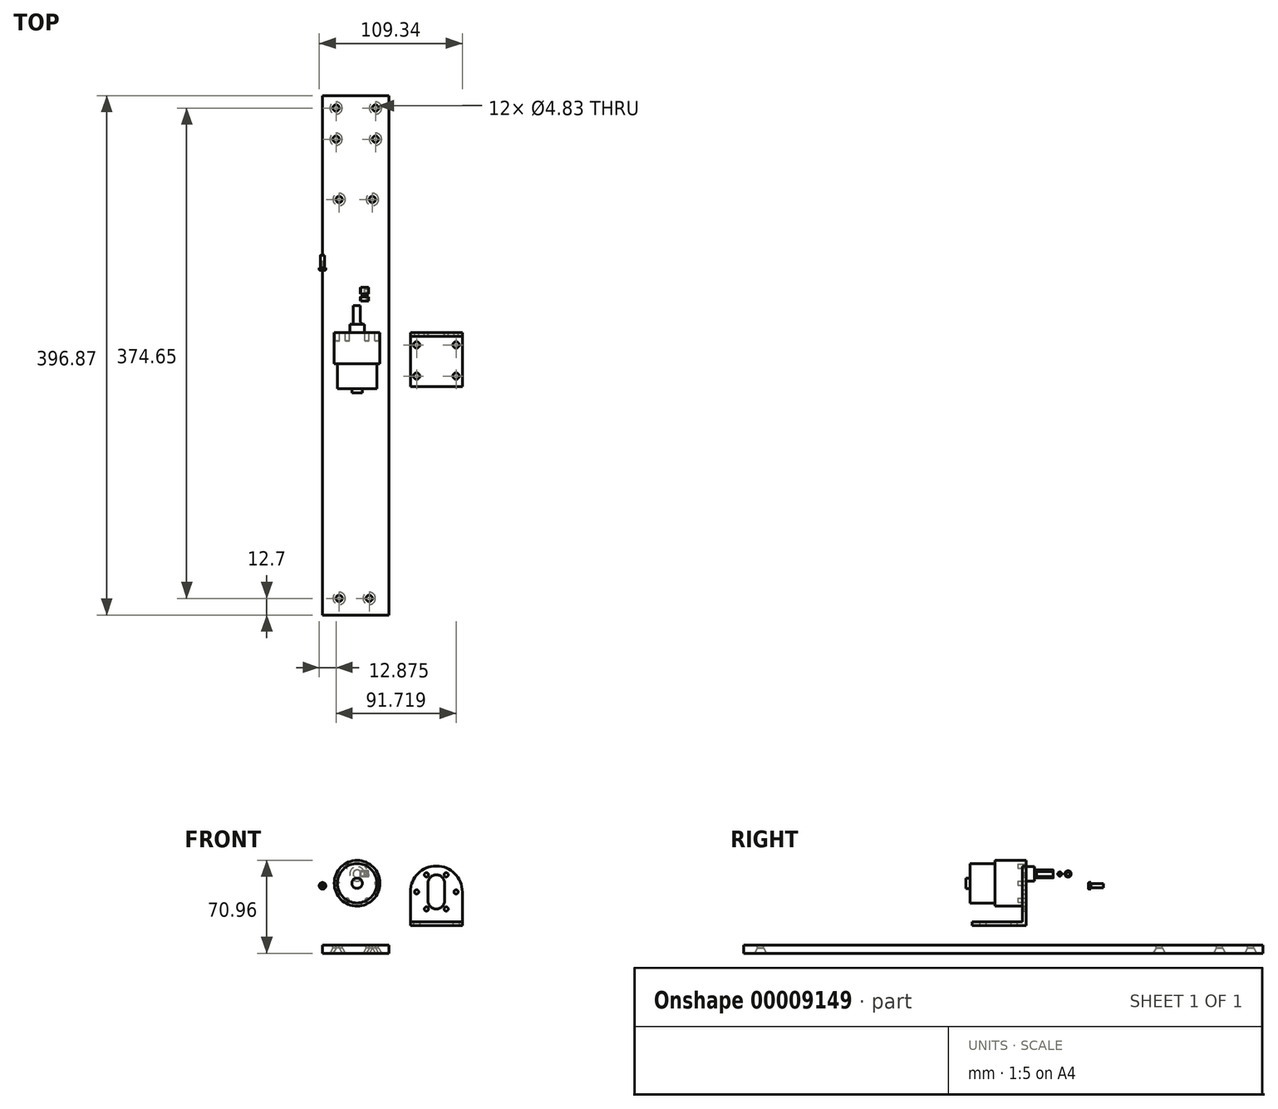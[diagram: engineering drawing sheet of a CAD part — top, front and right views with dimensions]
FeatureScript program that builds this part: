
annotation { "Feature Type Name" : "Feature", "Feature Type Description" : "" }
export const myFeature = defineFeature(function(context is Context, id is Id, definition is map)
    precondition{}
    {
        {
            var Q0;
            Q0=qCreatedBy(makeId("Front.planeOp"),FACE);
            var sketch = newSketch(context, id + "F0", { "sketchPlane" : qUnion([Q0])});
            skLineSegment(sketch, "E0.bottom", {"start": v(-48.57, -39.08) * mm, "end": v(2.23, -39.08) * mm});
            skLineSegment(sketch, "E0.top", {"start": v(-48.57, -45.43) * mm, "end": v(2.23, -45.43) * mm});
            skLineSegment(sketch, "E0.left", {"start": v(-48.57, -39.08) * mm, "end": v(-48.57, -45.43) * mm});
            skLineSegment(sketch, "E0.right", {"start": v(2.23, -39.08) * mm, "end": v(2.23, -45.43) * mm});
            skSolve(sketch);
        }
        {
            var Q0;
            Q0=makeQuery(id+"F0.imprint","IMPRINT",FACE,{"disambiguationData":[TD([[makeQuery(id+"F0.imprint","IMPRINT",EDGE,{"derivedFrom":sQuery(id+"F0.wireOp",EDGE,"E0.bottom")}),-1.0]])]});
            extrude(context, id + "F1", {"entities" : qUnion([Q0]), "depth" : 215.9 * mm, "hasSecondDirection" : true, "secondDirectionOppositeDirection" : true, "secondDirectionDepth" : 180.97 * mm});
        }
        {
            var Q0;
            Q0=makeQuery(id+"F1.opExtrude","SWEPT_FACE",FACE,{"disambiguationData":[OSD([sQuery(id+"F0.wireOp",EDGE,"E0.bottom")])]});
            var sketch = newSketch(context, id + "F2", { "sketchPlane" : qUnion([Q0])});
            skCircle(sketch, "E1", {"center": v(-10.47, 101.6) * mm, "radius": 2.41 * mm});
            skCircle(sketch, "E2", {"center": v(-35.87, 101.6) * mm, "radius": 2.41 * mm});
            skCircle(sketch, "E3", {"center": v(-12.89, -203.2) * mm, "radius": 2.41 * mm});
            skCircle(sketch, "E4", {"center": v(-35.87, -203.2) * mm, "radius": 2.41 * mm});
            skSolve(sketch);
        }
        {
            var Q0;
            Q0=makeQuery(id+"F2.imprint","IMPRINT",FACE,{"disambiguationData":[TD([[makeQuery(id+"F2.imprint","IMPRINT",EDGE,{"derivedFrom":sQuery(id+"F2.wireOp",EDGE,"E3")}),1.0]])]});
            var Q1;
            Q1=makeQuery(id+"F2.imprint","IMPRINT",FACE,{"disambiguationData":[TD([[makeQuery(id+"F2.imprint","IMPRINT",EDGE,{"derivedFrom":sQuery(id+"F2.wireOp",EDGE,"E4")}),1.0]])]});
            var Q2;
            Q2=makeQuery(id+"F2.imprint","IMPRINT",FACE,{"disambiguationData":[TD([[makeQuery(id+"F2.imprint","IMPRINT",EDGE,{"derivedFrom":sQuery(id+"F2.wireOp",EDGE,"E1")}),1.0]])]});
            var Q3;
            Q3=makeQuery(id+"F2.imprint","IMPRINT",FACE,{"disambiguationData":[TD([[makeQuery(id+"F2.imprint","IMPRINT",EDGE,{"derivedFrom":sQuery(id+"F2.wireOp",EDGE,"E2")}),1.0]])]});
            extrude(context, id + "F3", {"entities" : qUnion([Q0, Q1, Q2, Q3]), "operationType" : NewBodyOperationType.REMOVE, "endBound" : BoundingType.THROUGH_ALL, "oppositeDirection" : true, "depth" : 25.4 * mm});
        }
        {
            var Q0;
            Q0=qCreatedBy(makeId("Front.planeOp"),FACE);
            var sketch = newSketch(context, id + "F4", { "sketchPlane" : qUnion([Q0])});
            skLineSegment(sketch, "E5", {"start": v(53.48, 17.64) * mm, "end": v(53.48, -28.14) * mm, "construction": true});
            skLineSegment(sketch, "E6", {"start": v(23.33, 16.98) * mm, "end": v(23.33, -27.48) * mm, "construction": true});
            skLineSegment(sketch, "E7", {"start": v(38.4, 18.33) * mm, "end": v(38.4, -27.69) * mm, "construction": true});
            skCircle(sketch, "E8.cCircle", {"center": v(38.4, 1.46) * mm, "radius": 13.06 * mm, "construction": true});
            skLineSegment(sketch, "E8.0", {"start": v(30.87, 14.51) * mm, "end": v(45.95, 14.51) * mm, "construction": true});
            skLineSegment(sketch, "E8.1", {"start": v(45.95, 14.51) * mm, "end": v(53.48, 1.46) * mm, "construction": true});
            skLineSegment(sketch, "E8.2", {"start": v(53.48, 1.46) * mm, "end": v(45.95, -11.6) * mm, "construction": true});
            skLineSegment(sketch, "E8.3", {"start": v(45.95, -11.6) * mm, "end": v(30.87, -11.6) * mm, "construction": true});
            skLineSegment(sketch, "E8.4", {"start": v(30.87, -11.6) * mm, "end": v(23.33, 1.46) * mm, "construction": true});
            skLineSegment(sketch, "E8.5", {"start": v(23.33, 1.46) * mm, "end": v(30.87, 14.51) * mm, "construction": true});
            skPoint(sketch, "E8.0.midPoint", {"position": v(38.4, 14.51) * mm});
            skLineSegment(sketch, "E9", {"start": v(53.48, 14.51) * mm, "end": v(23.33, 14.51) * mm, "construction": true});
            skLineSegment(sketch, "E10", {"start": v(53.48, -11.6) * mm, "end": v(23.33, -11.6) * mm, "construction": true});
            skLineSegment(sketch, "E11", {"start": v(53.48, 8.16) * mm, "end": v(23.33, 8.16) * mm, "construction": true});
            skLineSegment(sketch, "E12", {"start": v(53.48, -5.25) * mm, "end": v(23.33, -5.25) * mm, "construction": true});
            skArc(sketch, "E13", {"start": v(44.76, 8.16) * mm, "mid": v(38.4, 14.51) * mm, "end": v(32.06, 8.16) * mm});
            skLineSegment(sketch, "E14", {"start": v(58.23, 1.46) * mm, "end": v(58.23, -24.3) * mm});
            skLineSegment(sketch, "E15", {"start": v(58.23, -24.3) * mm, "end": v(18.58, -24.3) * mm});
            skLineSegment(sketch, "E16", {"start": v(18.58, -24.3) * mm, "end": v(18.58, 1.46) * mm});
            skCircle(sketch, "E17", {"center": v(38.4, 1.46) * mm, "radius": 19.82 * mm});
            skLineSegment(sketch, "E18", {"start": v(44.76, 8.16) * mm, "end": v(44.76, -5.25) * mm});
            skLineSegment(sketch, "E19", {"start": v(32.06, 8.16) * mm, "end": v(32.06, -5.25) * mm});
            skArc(sketch, "E20", {"start": v(32.06, -5.25) * mm, "mid": v(38.4, -11.6) * mm, "end": v(44.76, -5.25) * mm});
            skCircle(sketch, "E21", {"center": v(45.95, 14.51) * mm, "radius": 1.59 * mm});
            skCircle(sketch, "E22", {"center": v(30.87, 14.51) * mm, "radius": 1.59 * mm});
            skCircle(sketch, "E23", {"center": v(45.95, -11.6) * mm, "radius": 1.59 * mm});
            skCircle(sketch, "E24", {"center": v(53.48, 1.46) * mm, "radius": 1.59 * mm});
            skCircle(sketch, "E25", {"center": v(23.33, 1.46) * mm, "radius": 1.59 * mm});
            skCircle(sketch, "E26", {"center": v(30.87, -11.6) * mm, "radius": 1.59 * mm});
            skSolve(sketch);
        }
        {
            var Q0;
            {var subQ2=sQuery(id+"F4.wireOp",EDGE,"E14");Q0=makeQuery(id+"F4.imprint","IMPRINT",FACE,{"disambiguationData":[TD([[makeQuery(id+"F4.imprint","IMPRINT",EDGE,{"derivedFrom":subQ2}),-1.0]])]});}
            var Q1;
            Q1=makeQuery(id+"F4.imprint","IMPRINT",FACE,{"disambiguationData":[TD([[makeQuery(id+"F4.imprint","IMPRINT",EDGE,{"derivedFrom":sQuery(id+"F4.wireOp",EDGE,"E13")}),-1.0]])]});
            extrude(context, id + "F5", {"entities" : qUnion([Q0, Q1]), "depth" : 3 * mm});
        }
        {
            var Q0;
            Q0=makeQuery(id+"F5.opExtrude","CAP_FACE",FACE,{"disambiguationData":[OSD([sQuery(id+"F4.wireOp",EDGE,"E13"),sQuery(id+"F4.wireOp",EDGE,"E14"),sQuery(id+"F4.wireOp",EDGE,"E15"),sQuery(id+"F4.wireOp",EDGE,"E16"),sQuery(id+"F4.wireOp",EDGE,"E17"),sQuery(id+"F4.wireOp",EDGE,"E18"),sQuery(id+"F4.wireOp",EDGE,"E19"),sQuery(id+"F4.wireOp",EDGE,"E20"),sQuery(id+"F4.wireOp",EDGE,"E21"),sQuery(id+"F4.wireOp",EDGE,"E22"),sQuery(id+"F4.wireOp",EDGE,"E23"),sQuery(id+"F4.wireOp",EDGE,"E24"),sQuery(id+"F4.wireOp",EDGE,"E25"),sQuery(id+"F4.wireOp",EDGE,"E26")])],"isStart":false});
            var sketch = newSketch(context, id + "F6", { "sketchPlane" : qUnion([Q0])});
            skLineSegment(sketch, "E27", {"start": v(18.58, -21.3) * mm, "end": v(58.23, -21.3) * mm});
            skSolve(sketch);
        }
        {
            var Q0;
            {var subQ1=sQuery(id+"F6.wireOp",EDGE,"E27");Q0=makeQuery(id+"F6.imprint","IMPRINT",FACE,{"disambiguationData":[TD([[makeQuery(id+"F6.imprint","IMPRINT",EDGE,{"derivedFrom":subQ1}),-1.0]])]});}
            extrude(context, id + "F7", {"entities" : qUnion([Q0]), "operationType" : NewBodyOperationType.ADD, "depth" : 38.28 * mm});
        }
        {
            var Q0;
            {var subQ0=sQuery(id+"F4.wireOp",EDGE,"E15");Q0=makeQuery(id+"F7.boolean.opBoolean","MERGE",FACE,{"derivedFrom":[makeQuery(id+"F5.opExtrude","SWEPT_FACE",FACE,{"disambiguationData":[OSD([subQ0])]}),makeQuery(id+"F7.opExtrude","SWEPT_FACE",FACE,{"disambiguationData":[OSD([subQ0])]})]});}
            var sketch = newSketch(context, id + "F8", { "sketchPlane" : qUnion([Q0])});
            skLineSegment(sketch, "E28", {"start": v(23.33, 41.27) * mm, "end": v(23.33, 0) * mm, "construction": true});
            skLineSegment(sketch, "E29", {"start": v(53.48, 41.27) * mm, "end": v(53.48, 0) * mm, "construction": true});
            skLineSegment(sketch, "E30", {"start": v(18.58, 33.35) * mm, "end": v(58.23, 33.35) * mm, "construction": true});
            skLineSegment(sketch, "E31", {"start": v(18.58, 9.55) * mm, "end": v(58.23, 9.55) * mm, "construction": true});
            skCircle(sketch, "E32", {"center": v(23.33, 33.35) * mm, "radius": 2.41 * mm});
            skCircle(sketch, "E33", {"center": v(53.48, 33.35) * mm, "radius": 2.41 * mm});
            skCircle(sketch, "E34", {"center": v(53.48, 9.55) * mm, "radius": 2.41 * mm});
            skCircle(sketch, "E35", {"center": v(23.33, 9.55) * mm, "radius": 2.41 * mm});
            skSolve(sketch);
        }
        {
            var Q0;
            Q0=makeQuery(id+"F8.imprint","IMPRINT",FACE,{"disambiguationData":[TD([[makeQuery(id+"F8.imprint","IMPRINT",EDGE,{"derivedFrom":sQuery(id+"F8.wireOp",EDGE,"E32")}),1.0]])]});
            var Q1;
            Q1=makeQuery(id+"F8.imprint","IMPRINT",FACE,{"disambiguationData":[TD([[makeQuery(id+"F8.imprint","IMPRINT",EDGE,{"derivedFrom":sQuery(id+"F8.wireOp",EDGE,"E33")}),1.0]])]});
            var Q2;
            Q2=makeQuery(id+"F8.imprint","IMPRINT",FACE,{"disambiguationData":[TD([[makeQuery(id+"F8.imprint","IMPRINT",EDGE,{"derivedFrom":sQuery(id+"F8.wireOp",EDGE,"E34")}),1.0]])]});
            var Q3;
            Q3=makeQuery(id+"F8.imprint","IMPRINT",FACE,{"disambiguationData":[TD([[makeQuery(id+"F8.imprint","IMPRINT",EDGE,{"derivedFrom":sQuery(id+"F8.wireOp",EDGE,"E35")}),1.0]])]});
            extrude(context, id + "F9", {"entities" : qUnion([Q0, Q1, Q2, Q3]), "operationType" : NewBodyOperationType.REMOVE, "endBound" : BoundingType.THROUGH_ALL, "oppositeDirection" : true, "depth" : 25.4 * mm});
        }
        {
            var Q0;
            Q0=qCreatedBy(makeId("Front.planeOp"),FACE);
            var sketch = newSketch(context, id + "F10", { "sketchPlane" : qUnion([Q0])});
            skCircle(sketch, "E36", {"center": v(-22.17, 8.07) * mm, "radius": 17.46 * mm});
            skSolve(sketch);
        }
        {
            var Q0;
            Q0=makeQuery(id+"F10.imprint","IMPRINT",FACE,{"disambiguationData":[TD([[makeQuery(id+"F10.imprint","IMPRINT",EDGE,{"derivedFrom":sQuery(id+"F10.wireOp",EDGE,"E36")}),1.0]])]});
            extrude(context, id + "F11", {"entities" : qUnion([Q0]), "depth" : 23.8 * mm});
        }
        {
            var Q0;
            Q0=makeQuery(id+"F11.opExtrude","CAP_FACE",FACE,{"disambiguationData":[OSD([sQuery(id+"F10.wireOp",EDGE,"E36")])],"isStart":true});
            var sketch = newSketch(context, id + "F12", { "sketchPlane" : qUnion([Q0])});
            skLineSegment(sketch, "E37", {"start": v(7.1, 16.89) * mm, "end": v(7.1, -0.74) * mm, "construction": true});
            skLineSegment(sketch, "E38", {"start": v(37.24, 16.89) * mm, "end": v(37.24, -0.74) * mm, "construction": true});
            skCircle(sketch, "E39.cCircle", {"center": v(22.17, 8.07) * mm, "radius": 13.06 * mm, "construction": true});
            skLineSegment(sketch, "E39.0", {"start": v(14.63, 21.13) * mm, "end": v(29.7, 21.13) * mm, "construction": true});
            skLineSegment(sketch, "E39.1", {"start": v(29.7, 21.13) * mm, "end": v(37.24, 8.07) * mm, "construction": true});
            skLineSegment(sketch, "E39.2", {"start": v(37.24, 8.07) * mm, "end": v(29.7, -4.98) * mm, "construction": true});
            skLineSegment(sketch, "E39.3", {"start": v(29.7, -4.98) * mm, "end": v(14.63, -4.98) * mm, "construction": true});
            skLineSegment(sketch, "E39.4", {"start": v(14.63, -4.98) * mm, "end": v(7.1, 8.07) * mm, "construction": true});
            skLineSegment(sketch, "E39.5", {"start": v(7.1, 8.07) * mm, "end": v(14.63, 21.13) * mm, "construction": true});
            skPoint(sketch, "E39.0.midPoint", {"position": v(22.17, 21.13) * mm});
            skCircle(sketch, "E40", {"center": v(14.63, 21.13) * mm, "radius": 1.59 * mm});
            skCircle(sketch, "E41", {"center": v(29.7, 21.13) * mm, "radius": 1.59 * mm});
            skCircle(sketch, "E42", {"center": v(37.24, 8.07) * mm, "radius": 1.59 * mm});
            skCircle(sketch, "E43", {"center": v(29.7, -4.98) * mm, "radius": 1.59 * mm});
            skCircle(sketch, "E44", {"center": v(14.63, -4.98) * mm, "radius": 1.59 * mm});
            skCircle(sketch, "E45", {"center": v(7.1, 8.07) * mm, "radius": 1.59 * mm});
            skLineSegment(sketch, "E46", {"start": v(22.17, 25.53) * mm, "end": v(22.17, -9.4) * mm, "construction": true});
            skSolve(sketch);
        }
        {
            var Q0;
            Q0=makeQuery(id+"F12.imprint","IMPRINT",FACE,{"disambiguationData":[TD([[makeQuery(id+"F12.imprint","IMPRINT",EDGE,{"derivedFrom":sQuery(id+"F12.wireOp",EDGE,"E40")}),1.0]])]});
            var Q1;
            Q1=makeQuery(id+"F12.imprint","IMPRINT",FACE,{"disambiguationData":[TD([[makeQuery(id+"F12.imprint","IMPRINT",EDGE,{"derivedFrom":sQuery(id+"F12.wireOp",EDGE,"E41")}),1.0]])]});
            var Q2;
            Q2=makeQuery(id+"F12.imprint","IMPRINT",FACE,{"disambiguationData":[TD([[makeQuery(id+"F12.imprint","IMPRINT",EDGE,{"derivedFrom":sQuery(id+"F12.wireOp",EDGE,"E42")}),1.0]])]});
            var Q3;
            Q3=makeQuery(id+"F12.imprint","IMPRINT",FACE,{"disambiguationData":[TD([[makeQuery(id+"F12.imprint","IMPRINT",EDGE,{"derivedFrom":sQuery(id+"F12.wireOp",EDGE,"E43")}),1.0]])]});
            var Q4;
            Q4=makeQuery(id+"F12.imprint","IMPRINT",FACE,{"disambiguationData":[TD([[makeQuery(id+"F12.imprint","IMPRINT",EDGE,{"derivedFrom":sQuery(id+"F12.wireOp",EDGE,"E44")}),1.0]])]});
            var Q5;
            Q5=makeQuery(id+"F12.imprint","IMPRINT",FACE,{"disambiguationData":[TD([[makeQuery(id+"F12.imprint","IMPRINT",EDGE,{"derivedFrom":sQuery(id+"F12.wireOp",EDGE,"E45")}),1.0]])]});
            extrude(context, id + "F13", {"entities" : qUnion([Q0, Q1, Q2, Q3, Q4, Q5]), "operationType" : NewBodyOperationType.REMOVE, "oppositeDirection" : true, "depth" : 6.35 * mm});
        }
        {
            var Q0;
            Q0=makeQuery(id+"F11.opExtrude","CAP_FACE",FACE,{"disambiguationData":[OSD([sQuery(id+"F10.wireOp",EDGE,"E36")])],"isStart":true});
            var sketch = newSketch(context, id + "F14", { "sketchPlane" : qUnion([Q0])});
            skLineSegment(sketch, "E47", {"start": v(6.24, 15.22) * mm, "end": v(38.1, 15.22) * mm, "construction": true});
            skLineSegment(sketch, "E48", {"start": v(22.17, 15.22) * mm, "end": v(22.17, 25.53) * mm, "construction": true});
            skCircle(sketch, "E49", {"center": v(22.17, 15.22) * mm, "radius": 5.55 * mm});
            skSolve(sketch);
        }
        {
            var Q0;
            Q0=makeQuery(id+"F14.imprint","IMPRINT",FACE,{"disambiguationData":[TD([[makeQuery(id+"F14.imprint","IMPRINT",EDGE,{"derivedFrom":sQuery(id+"F14.wireOp",EDGE,"E49")}),1.0]])]});
            extrude(context, id + "F15", {"entities" : qUnion([Q0]), "operationType" : NewBodyOperationType.ADD, "depth" : 6.35 * mm});
        }
        {
            var Q0;
            Q0=makeQuery(id+"F15.opExtrude","CAP_FACE",FACE,{"disambiguationData":[OSD([sQuery(id+"F14.wireOp",EDGE,"E49")])],"isStart":false});
            var sketch = newSketch(context, id + "F16", { "sketchPlane" : qUnion([Q0])});
            skCircle(sketch, "E50", {"center": v(22.17, 15.22) * mm, "radius": 3 * mm});
            skSolve(sketch);
        }
        {
            var Q0;
            Q0=makeQuery(id+"F16.imprint","IMPRINT",FACE,{"disambiguationData":[TD([[makeQuery(id+"F16.imprint","IMPRINT",EDGE,{"derivedFrom":sQuery(id+"F16.wireOp",EDGE,"E50")}),1.0]])]});
            extrude(context, id + "F17", {"entities" : qUnion([Q0]), "operationType" : NewBodyOperationType.ADD, "depth" : 14.27 * mm});
        }
        {
            var Q0;
            Q0=makeQuery(id+"F11.opExtrude","CAP_FACE",FACE,{"disambiguationData":[OSD([sQuery(id+"F10.wireOp",EDGE,"E36")])],"isStart":false});
            var sketch = newSketch(context, id + "F18", { "sketchPlane" : qUnion([Q0])});
            skCircle(sketch, "E51", {"center": v(-22.17, 8.07) * mm, "radius": 15.07 * mm});
            skSolve(sketch);
        }
        {
            var Q0;
            Q0=makeQuery(id+"F18.imprint","IMPRINT",FACE,{"disambiguationData":[TD([[makeQuery(id+"F18.imprint","IMPRINT",EDGE,{"derivedFrom":sQuery(id+"F18.wireOp",EDGE,"E51")}),1.0]])]});
            extrude(context, id + "F19", {"entities" : qUnion([Q0]), "operationType" : NewBodyOperationType.ADD, "depth" : 19.05 * mm});
        }
        {
            var Q0;
            Q0=makeQuery(id+"F19.opExtrude","CAP_FACE",FACE,{"disambiguationData":[OSD([sQuery(id+"F18.wireOp",EDGE,"E51")])],"isStart":false});
            var sketch = newSketch(context, id + "F20", { "sketchPlane" : qUnion([Q0])});
            skCircle(sketch, "E52", {"center": v(-22.17, 8.07) * mm, "radius": 3.96 * mm});
            skSolve(sketch);
        }
        {
            var Q0;
            Q0=makeQuery(id+"F20.imprint","IMPRINT",FACE,{"disambiguationData":[TD([[makeQuery(id+"F20.imprint","IMPRINT",EDGE,{"derivedFrom":sQuery(id+"F20.wireOp",EDGE,"E52")}),1.0]])]});
            extrude(context, id + "F21", {"entities" : qUnion([Q0]), "operationType" : NewBodyOperationType.ADD, "depth" : 3.17 * mm});
        }
        {
            var Q0;
            Q0=makeQuery(id+"F3.boolean.opBoolean","INTERSECT",EDGE,{"derivedFrom":[makeQuery(id+"F1.opExtrude","SWEPT_FACE",FACE,{"disambiguationData":[OSD([sQuery(id+"F0.wireOp",EDGE,"E0.top")])]}),makeQuery(id+"F3.opExtrude","SWEPT_FACE",FACE,{"disambiguationData":[OSD([sQuery(id+"F2.wireOp",EDGE,"E3")])]})]});
            var Q1;
            Q1=makeQuery(id+"F3.boolean.opBoolean","INTERSECT",EDGE,{"derivedFrom":[makeQuery(id+"F1.opExtrude","SWEPT_FACE",FACE,{"disambiguationData":[OSD([sQuery(id+"F0.wireOp",EDGE,"E0.top")])]}),makeQuery(id+"F3.opExtrude","SWEPT_FACE",FACE,{"disambiguationData":[OSD([sQuery(id+"F2.wireOp",EDGE,"E4")])]})]});
            var Q2;
            Q2=makeQuery(id+"F3.boolean.opBoolean","INTERSECT",EDGE,{"derivedFrom":[makeQuery(id+"F1.opExtrude","SWEPT_FACE",FACE,{"disambiguationData":[OSD([sQuery(id+"F0.wireOp",EDGE,"E0.top")])]}),makeQuery(id+"F3.opExtrude","SWEPT_FACE",FACE,{"disambiguationData":[OSD([sQuery(id+"F2.wireOp",EDGE,"E1")])]})]});
            var Q3;
            Q3=makeQuery(id+"F3.boolean.opBoolean","INTERSECT",EDGE,{"derivedFrom":[makeQuery(id+"F1.opExtrude","SWEPT_FACE",FACE,{"disambiguationData":[OSD([sQuery(id+"F0.wireOp",EDGE,"E0.top")])]}),makeQuery(id+"F3.opExtrude","SWEPT_FACE",FACE,{"disambiguationData":[OSD([sQuery(id+"F2.wireOp",EDGE,"E2")])]})]});
            chamfer(context, id + "F22", {"entities" : qUnion([Q0, Q1, Q2, Q3]), "chamferType" : ChamferType.OFFSET_ANGLE, "width" : 2.3 * mm, "oppositeDirection" : false, "angle" : 60 * degree, "tangentPropagation" : true});
        }
        {
            var Q0;
            Q0=makeQuery(id+"F1.opExtrude","SWEPT_FACE",FACE,{"disambiguationData":[OSD([sQuery(id+"F0.wireOp",EDGE,"E0.bottom")])]});
            var sketch = newSketch(context, id + "F23", { "sketchPlane" : qUnion([Q0])});
            skLineSegment(sketch, "E53", {"start": v(-23.17, 180.98) * mm, "end": v(-23.17, 91.89) * mm, "construction": true});
            skLineSegment(sketch, "E54", {"start": v(2.23, 171.45) * mm, "end": v(-48.57, 171.45) * mm, "construction": true});
            skLineSegment(sketch, "E55", {"start": v(2.23, 147.65) * mm, "end": v(-48.57, 147.65) * mm, "construction": true});
            skLineSegment(sketch, "E56", {"start": v(-8.11, 180.98) * mm, "end": v(-8.11, 120.47) * mm, "construction": true});
            skLineSegment(sketch, "E57", {"start": v(-38.24, 180.98) * mm, "end": v(-38.24, 116.54) * mm, "construction": true});
            skCircle(sketch, "E58", {"center": v(-8.11, 171.45) * mm, "radius": 2.41 * mm});
            skCircle(sketch, "E59", {"center": v(-8.11, 147.65) * mm, "radius": 2.41 * mm});
            skCircle(sketch, "E60", {"center": v(-38.24, 147.65) * mm, "radius": 2.41 * mm});
            skCircle(sketch, "E61", {"center": v(-38.24, 171.45) * mm, "radius": 2.41 * mm});
            skSolve(sketch);
        }
        {
            var Q0;
            Q0=makeQuery(id+"F23.imprint","IMPRINT",FACE,{"disambiguationData":[TD([[makeQuery(id+"F23.imprint","IMPRINT",EDGE,{"derivedFrom":sQuery(id+"F23.wireOp",EDGE,"E58")}),1.0]])]});
            var Q1;
            Q1=makeQuery(id+"F23.imprint","IMPRINT",FACE,{"disambiguationData":[TD([[makeQuery(id+"F23.imprint","IMPRINT",EDGE,{"derivedFrom":sQuery(id+"F23.wireOp",EDGE,"E59")}),1.0]])]});
            var Q2;
            Q2=makeQuery(id+"F23.imprint","IMPRINT",FACE,{"disambiguationData":[TD([[makeQuery(id+"F23.imprint","IMPRINT",EDGE,{"derivedFrom":sQuery(id+"F23.wireOp",EDGE,"E60")}),1.0]])]});
            var Q3;
            Q3=makeQuery(id+"F23.imprint","IMPRINT",FACE,{"disambiguationData":[TD([[makeQuery(id+"F23.imprint","IMPRINT",EDGE,{"derivedFrom":sQuery(id+"F23.wireOp",EDGE,"E61")}),1.0]])]});
            extrude(context, id + "F24", {"entities" : qUnion([Q0, Q1, Q2, Q3]), "operationType" : NewBodyOperationType.REMOVE, "endBound" : BoundingType.THROUGH_ALL, "oppositeDirection" : true, "depth" : 25.4 * mm});
        }
        {
            var Q0;
            Q0=makeQuery(id+"F24.boolean.opBoolean","INTERSECT",EDGE,{"derivedFrom":[makeQuery(id+"F1.opExtrude","SWEPT_FACE",FACE,{"disambiguationData":[OSD([sQuery(id+"F0.wireOp",EDGE,"E0.top")])]}),makeQuery(id+"F24.opExtrude","SWEPT_FACE",FACE,{"disambiguationData":[OSD([sQuery(id+"F23.wireOp",EDGE,"E61")])]})]});
            var Q1;
            Q1=makeQuery(id+"F24.boolean.opBoolean","INTERSECT",EDGE,{"derivedFrom":[makeQuery(id+"F1.opExtrude","SWEPT_FACE",FACE,{"disambiguationData":[OSD([sQuery(id+"F0.wireOp",EDGE,"E0.top")])]}),makeQuery(id+"F24.opExtrude","SWEPT_FACE",FACE,{"disambiguationData":[OSD([sQuery(id+"F23.wireOp",EDGE,"E60")])]})]});
            var Q2;
            Q2=makeQuery(id+"F24.boolean.opBoolean","INTERSECT",EDGE,{"derivedFrom":[makeQuery(id+"F1.opExtrude","SWEPT_FACE",FACE,{"disambiguationData":[OSD([sQuery(id+"F0.wireOp",EDGE,"E0.top")])]}),makeQuery(id+"F24.opExtrude","SWEPT_FACE",FACE,{"disambiguationData":[OSD([sQuery(id+"F23.wireOp",EDGE,"E59")])]})]});
            var Q3;
            Q3=makeQuery(id+"F24.boolean.opBoolean","INTERSECT",EDGE,{"derivedFrom":[makeQuery(id+"F1.opExtrude","SWEPT_FACE",FACE,{"disambiguationData":[OSD([sQuery(id+"F0.wireOp",EDGE,"E0.top")])]}),makeQuery(id+"F24.opExtrude","SWEPT_FACE",FACE,{"disambiguationData":[OSD([sQuery(id+"F23.wireOp",EDGE,"E58")])]})]});
            chamfer(context, id + "F25", {"entities" : qUnion([Q0, Q1, Q2, Q3]), "chamferType" : ChamferType.OFFSET_ANGLE, "width" : 2.3 * mm, "oppositeDirection" : false, "angle" : 60 * degree, "tangentPropagation" : true});
        }
        {
            var Q0;
            Q0=makeQuery(id+"F1.opExtrude","SWEPT_FACE",FACE,{"disambiguationData":[OSD([sQuery(id+"F0.wireOp",EDGE,"E0.left")])]});
            var sketch = newSketch(context, id + "F26", { "sketchPlane" : qUnion([Q0])});
            skLineSegment(sketch, "E62.bottom", {"start": v(-58.98, 6.07) * mm, "end": v(-49.46, 6.07) * mm});
            skLineSegment(sketch, "E62.top", {"start": v(-58.98, 4.5) * mm, "end": v(-49.46, 4.5) * mm});
            skLineSegment(sketch, "E62.left", {"start": v(-58.98, 6.07) * mm, "end": v(-58.98, 4.5) * mm});
            skLineSegment(sketch, "E63", {"start": v(-49.46, 6.07) * mm, "end": v(-48.19, 6.07) * mm});
            skLineSegment(sketch, "E64", {"start": v(-48.19, 6.07) * mm, "end": v(-48.19, 3.53) * mm});
            skLineSegment(sketch, "E65", {"start": v(-48.19, 3.53) * mm, "end": v(-49.46, 3.53) * mm});
            skLineSegment(sketch, "E66", {"start": v(-49.46, 3.53) * mm, "end": v(-49.46, 4.5) * mm});
            skSolve(sketch);
        }
        {
            var Q0;
            Q0=makeQuery(id+"F26.imprint","IMPRINT",FACE,{"disambiguationData":[TD([[makeQuery(id+"F26.imprint","IMPRINT",EDGE,{"derivedFrom":sQuery(id+"F26.wireOp",EDGE,"E62.bottom")}),-1.0]])]});
            var Q1;
            Q1=sQuery(id+"F26.wireOp",EDGE,"E62.bottom");
            revolve(context, id + "F27", {"entities" : qUnion([Q0]), "axis" : qUnion([Q1]), "revolveType" : RevolveType.FULL});
        }
        {
            var Q0;
            Q0=makeQuery(id+"F27.opRevolve","SWEPT_FACE",FACE,{"disambiguationData":[OSD([sQuery(id+"F26.wireOp",EDGE,"E64")])]});
            var sketch = newSketch(context, id + "F28", { "sketchPlane" : qUnion([Q0])});
            skLineSegment(sketch, "E67", {"start": v(-51.08, 6.47) * mm, "end": v(-46.06, 6.47) * mm});
            skLineSegment(sketch, "E68", {"start": v(-51.08, 5.68) * mm, "end": v(-46.06, 5.68) * mm});
            skSolve(sketch);
        }
        {
            var Q0;
            {var subQ1=sQuery(id+"F28.wireOp",EDGE,"E67");Q0=makeQuery(id+"F28.imprint","IMPRINT",FACE,{"disambiguationData":[TD([[makeQuery(id+"F28.imprint","IMPRINT",EDGE,{"derivedFrom":subQ1}),1.0]])]});}
            var Q1;
            {var subQ1=sQuery(id+"F28.wireOp",EDGE,"E68");Q1=makeQuery(id+"F28.imprint","IMPRINT",FACE,{"disambiguationData":[TD([[makeQuery(id+"F28.imprint","IMPRINT",EDGE,{"derivedFrom":subQ1}),-1.0]])]});}
            extrude(context, id + "F29", {"entities" : qUnion([Q0, Q1]), "operationType" : NewBodyOperationType.ADD, "depth" : 0.79 * mm});
        }
        {
            var Q0;
            {var subQ0=sQuery(id+"F26.wireOp",EDGE,"E64");var subQ1=sQuery(id+"F26.wireOp",EDGE,"E65");var subQ2=makeQuery(id+"F27.opRevolve","SWEPT_EDGE",EDGE,{"disambiguationData":[OSD([subQ0,subQ1])]});var subQ3=sQuery(id+"F28.wireOp",EDGE,"E67");Q0=makeQuery(id+"F29.opExtrude","CAP_EDGE",EDGE,{"disambiguationData":[OSD([subQ0,subQ1]),TDD([makeQuery(id+"F28.imprint","IMPRINT",EDGE,{"disambiguationData":[TD([[makeQuery(id+"F28.imprint","INTERSECT",VERTEX,{"disambiguationData":[OD(0.0)],"derivedFrom":[subQ2,subQ3]}),-1.0]])],"derivedFrom":subQ2})])],"isStart":false});}
            var Q1;
            {var subQ0=sQuery(id+"F26.wireOp",EDGE,"E64");var subQ1=sQuery(id+"F26.wireOp",EDGE,"E65");var subQ2=makeQuery(id+"F27.opRevolve","SWEPT_EDGE",EDGE,{"disambiguationData":[OSD([subQ0,subQ1])]});var subQ3=sQuery(id+"F28.wireOp",EDGE,"E68");Q1=makeQuery(id+"F29.opExtrude","CAP_EDGE",EDGE,{"disambiguationData":[OSD([subQ0,subQ1]),TDD([makeQuery(id+"F28.imprint","IMPRINT",EDGE,{"disambiguationData":[TD([[makeQuery(id+"F28.imprint","INTERSECT",VERTEX,{"disambiguationData":[OD(0.0)],"derivedFrom":[subQ2,subQ3]}),1.0]])],"derivedFrom":subQ2})])],"isStart":false});}
            fillet(context, id + "F30", {"entities" : qUnion([Q0, Q1]), "radius" : 0.76 * mm, "tangentPropagation" : true, "allowEdgeOverflow" : false});
        }
        {
            var Q0;
            Q0=makeQuery(id+"F17.opExtrude","CAP_FACE",FACE,{"disambiguationData":[OSD([sQuery(id+"F16.wireOp",EDGE,"E50")])],"isStart":false});
            var sketch = newSketch(context, id + "F31", { "sketchPlane" : qUnion([Q0])});
            skCircle(sketch, "E69", {"center": v(22.17, 15.22) * mm, "radius": 3.03 * mm});
            skLineSegment(sketch, "E70", {"start": v(19.85, 17.13) * mm, "end": v(19.85, 13.32) * mm});
            skSolve(sketch);
        }
        {
            var Q0;
            {var subQ1=sQuery(id+"F31.wireOp",EDGE,"E70");Q0=makeQuery(id+"F31.imprint","IMPRINT",FACE,{"disambiguationData":[TD([[makeQuery(id+"F31.imprint","IMPRINT",EDGE,{"derivedFrom":subQ1}),-1.0]])]});}
            extrude(context, id + "F32", {"entities" : qUnion([Q0]), "operationType" : NewBodyOperationType.REMOVE, "oppositeDirection" : true, "depth" : 12.7 * mm});
        }
        {
            var Q0;
            Q0=makeQuery(id+"F32.boolean.opBoolean","COPY",FACE,{"derivedFrom":makeQuery(id+"F32.opExtrude","SWEPT_FACE",FACE,{"disambiguationData":[OSD([sQuery(id+"F31.wireOp",EDGE,"E70")])]})});
            var sketch = newSketch(context, id + "F33", { "sketchPlane" : qUnion([Q0])});
            skCircle(sketch, "E71", {"center": v(25.65, 15.1) * mm, "radius": 1.59 * mm});
            skSolve(sketch);
        }
        {
            var Q0;
            Q0=makeQuery(id+"F33.imprint","IMPRINT",FACE,{"disambiguationData":[TD([[makeQuery(id+"F33.imprint","IMPRINT",EDGE,{"derivedFrom":sQuery(id+"F33.wireOp",EDGE,"E71")}),1.0]])]});
            extrude(context, id + "F34", {"entities" : qUnion([Q0]), "depth" : 6.35 * mm});
        }
        {
            var Q0;
            Q0=makeQuery(id+"F34.opExtrude","CAP_FACE",FACE,{"disambiguationData":[OSD([sQuery(id+"F33.wireOp",EDGE,"E71")])],"isStart":false});
            var sketch = newSketch(context, id + "F35", { "sketchPlane" : qUnion([Q0])});
            skCircle(sketch, "E72.cCircle", {"center": v(25.65, 15.1) * mm, "radius": 1.02 * mm, "construction": true});
            skLineSegment(sketch, "E72.0", {"start": v(25.06, 16.1) * mm, "end": v(26.24, 16.1) * mm});
            skLineSegment(sketch, "E72.1", {"start": v(26.24, 16.1) * mm, "end": v(26.82, 15.1) * mm});
            skLineSegment(sketch, "E72.2", {"start": v(26.82, 15.1) * mm, "end": v(26.24, 14.07) * mm});
            skLineSegment(sketch, "E72.3", {"start": v(26.24, 14.07) * mm, "end": v(25.06, 14.07) * mm});
            skLineSegment(sketch, "E72.4", {"start": v(25.06, 14.07) * mm, "end": v(24.48, 15.1) * mm});
            skLineSegment(sketch, "E72.5", {"start": v(24.48, 15.1) * mm, "end": v(25.06, 16.1) * mm});
            skPoint(sketch, "E72.0.midPoint", {"position": v(25.65, 16.1) * mm});
            skSolve(sketch);
        }
        {
            var Q0;
            Q0=makeQuery(id+"F35.imprint","IMPRINT",FACE,{"disambiguationData":[TD([[makeQuery(id+"F35.imprint","IMPRINT",EDGE,{"derivedFrom":sQuery(id+"F35.wireOp",EDGE,"E72.0")}),-1.0]])]});
            extrude(context, id + "F36", {"entities" : qUnion([Q0]), "operationType" : NewBodyOperationType.REMOVE, "oppositeDirection" : true, "depth" : 1.57 * mm});
        }
        {
            var Q0;
            Q0=makeQuery(id+"F34.opExtrude","CAP_EDGE",EDGE,{"disambiguationData":[OSD([sQuery(id+"F33.wireOp",EDGE,"E71")])],"isStart":true});
            chamfer(context, id + "F37", {"entities" : qUnion([Q0]), "width" : 0.5 * mm, "tangentPropagation" : true});
        }
        {
            var Q0;
            Q0=makeQuery(id+"F32.boolean.opBoolean","COPY",FACE,{"derivedFrom":makeQuery(id+"F32.opExtrude","SWEPT_FACE",FACE,{"disambiguationData":[OSD([sQuery(id+"F31.wireOp",EDGE,"E70")])]})});
            var sketch = newSketch(context, id + "F38", { "sketchPlane" : qUnion([Q0])});
            skCircle(sketch, "E73", {"center": v(31.91, 15.19) * mm, "radius": 2.41 * mm});
            skSolve(sketch);
        }
        {
            var Q0;
            Q0=makeQuery(id+"F38.imprint","IMPRINT",FACE,{"disambiguationData":[TD([[makeQuery(id+"F38.imprint","IMPRINT",EDGE,{"derivedFrom":sQuery(id+"F38.wireOp",EDGE,"E73")}),1.0]])]});
            extrude(context, id + "F39", {"entities" : qUnion([Q0]), "depth" : 6.35 * mm});
        }
        {
            var Q0;
            Q0=makeQuery(id+"F39.opExtrude","CAP_FACE",FACE,{"disambiguationData":[OSD([sQuery(id+"F38.wireOp",EDGE,"E73")])],"isStart":false});
            var sketch = newSketch(context, id + "F40", { "sketchPlane" : qUnion([Q0])});
            skCircle(sketch, "E74.cCircle", {"center": v(31.91, 15.19) * mm, "radius": 1.59 * mm, "construction": true});
            skLineSegment(sketch, "E74.0", {"start": v(31, 16.77) * mm, "end": v(32.83, 16.77) * mm});
            skLineSegment(sketch, "E74.1", {"start": v(32.83, 16.77) * mm, "end": v(33.75, 15.19) * mm});
            skLineSegment(sketch, "E74.2", {"start": v(33.75, 15.19) * mm, "end": v(32.83, 13.6) * mm});
            skLineSegment(sketch, "E74.3", {"start": v(32.83, 13.6) * mm, "end": v(31, 13.6) * mm});
            skLineSegment(sketch, "E74.4", {"start": v(31, 13.6) * mm, "end": v(30.08, 15.19) * mm});
            skLineSegment(sketch, "E74.5", {"start": v(30.08, 15.19) * mm, "end": v(31, 16.77) * mm});
            skPoint(sketch, "E74.0.midPoint", {"position": v(31.91, 16.77) * mm});
            skSolve(sketch);
        }
        {
            var Q0;
            Q0=makeQuery(id+"F40.imprint","IMPRINT",FACE,{"disambiguationData":[TD([[makeQuery(id+"F40.imprint","IMPRINT",EDGE,{"derivedFrom":sQuery(id+"F40.wireOp",EDGE,"E74.0")}),-1.0]])]});
            extrude(context, id + "F41", {"entities" : qUnion([Q0]), "operationType" : NewBodyOperationType.REMOVE, "oppositeDirection" : true, "depth" : 3.17 * mm});
        }
        {
            var Q0;
            Q0=makeQuery(id+"F39.opExtrude","CAP_EDGE",EDGE,{"disambiguationData":[OSD([sQuery(id+"F38.wireOp",EDGE,"E73")])],"isStart":true});
            chamfer(context, id + "F42", {"entities" : qUnion([Q0]), "width" : 0.5 * mm, "tangentPropagation" : true});
        }
    });
